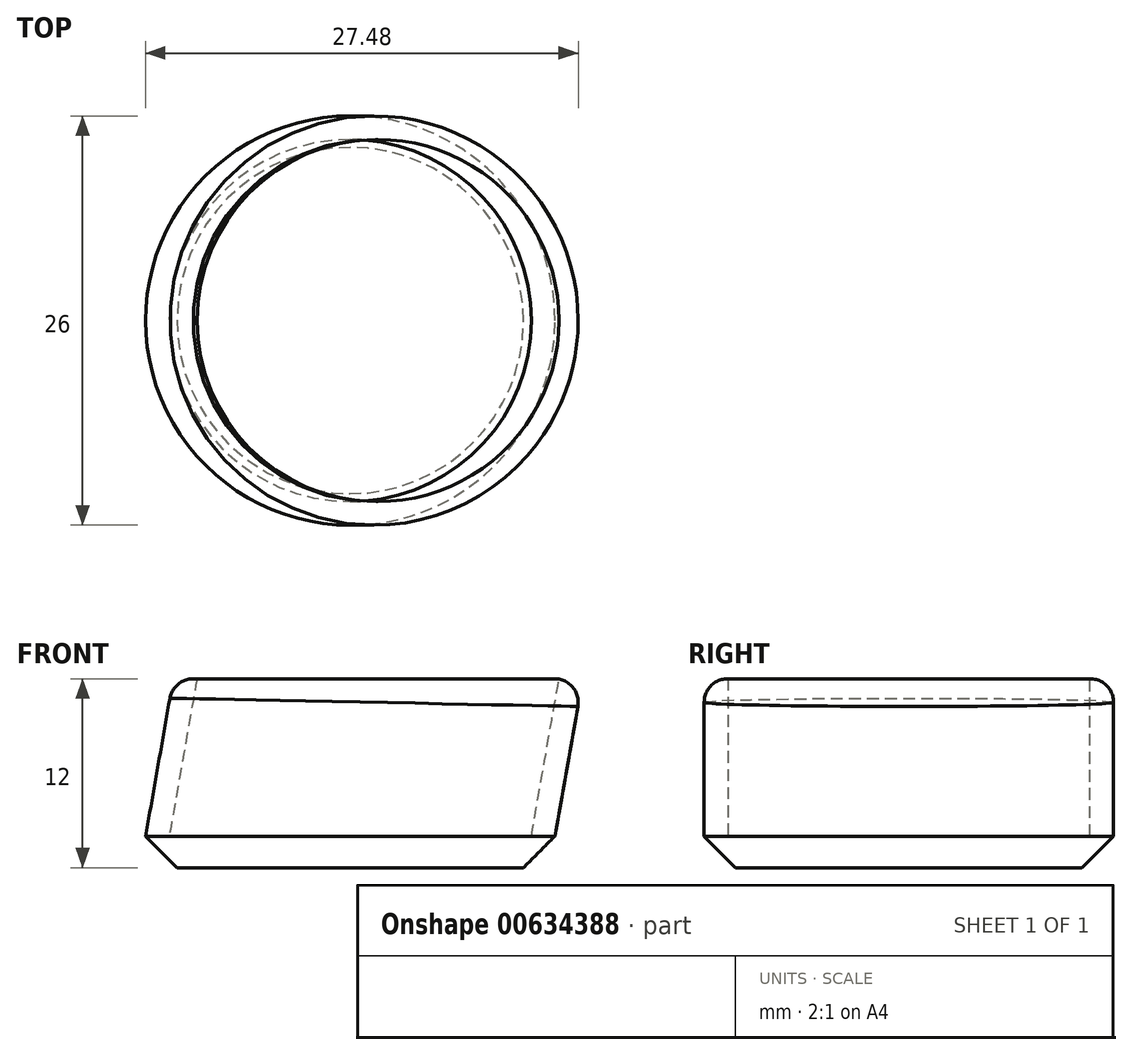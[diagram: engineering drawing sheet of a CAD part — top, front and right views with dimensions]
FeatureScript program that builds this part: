
annotation { "Feature Type Name" : "Feature", "Feature Type Description" : "" }
export const myFeature = defineFeature(function(context is Context, id is Id, definition is map)
    precondition{}
    {
        {
            var Q0;
            Q0=qCreatedBy(makeId("Front.planeOp"),FACE);
            var sketch = newSketch(context, id + "F0", { "sketchPlane" : qUnion([Q0])});
            skLineSegment(sketch, "E0", {"start": v(0, 0) * mm, "end": v(1.76, 10) * mm});
            skLineSegment(sketch, "E1", {"start": v(0, 0) * mm, "end": v(0, 10) * mm, "construction": true});
            skLineSegment(sketch, "E2", {"start": v(0, 10) * mm, "end": v(1.76, 10) * mm, "construction": true});
            skSolve(sketch);
        }
        {
            var Q0;
            Q0=qCreatedBy(makeId("Top.planeOp"),FACE);
            var sketch = newSketch(context, id + "F1", { "sketchPlane" : qUnion([Q0])});
            skCircle(sketch, "E3", {"center": v(0, 0) * mm, "radius": 13 * mm});
            skCircle(sketch, "E4", {"center": v(0, 0) * mm, "radius": 11.5 * mm});
            skSolve(sketch);
        }
        {
            var Q0;
            Q0=makeQuery(id+"F1.imprint","IMPRINT",FACE,{"disambiguationData":[TD([[makeQuery(id+"F1.imprint","IMPRINT",EDGE,{"derivedFrom":sQuery(id+"F1.wireOp",EDGE,"E3")}),1.0]])]});
            var Q1;
            Q1=sQuery(id+"F0.wireOp",EDGE,"E0");
            sweep(context, id + "F2", {"profiles" : qUnion([Q0]), "path" : qUnion([Q1])});
        }
        {
            var Q0;
            Q0=qCreatedBy(makeId("Top.planeOp"),FACE);
            var sketch = newSketch(context, id + "F3", { "sketchPlane" : qUnion([Q0])});
            skCircle(sketch, "E5.0", {"center": v(0, 0) * mm, "radius": 13 * mm});
            skSolve(sketch);
        }
        {
            var Q0;
            Q0=makeQuery(id+"F3.imprint","IMPRINT",FACE,{"disambiguationData":[TD([[makeQuery(id+"F3.imprint","IMPRINT",EDGE,{"derivedFrom":sQuery(id+"F3.wireOp",EDGE,"E5.0")}),1.0]])]});
            extrude(context, id + "F4", {"entities" : qUnion([Q0]), "operationType" : NewBodyOperationType.ADD, "oppositeDirection" : true, "depth" : 2 * mm, "offsetDistance" : 25 * mm});
        }
        {
            var Q0;
            Q0=makeQuery(id+"F2.opSweep","CAP_EDGE",EDGE,{"disambiguationData":[OSD([sQuery(id+"F0.wireOp",VERTEX,"E0.end"),sQuery(id+"F1.wireOp",EDGE,"E3")])],"isStart":false});
            fillet(context, id + "F5", {"entities" : qUnion([Q0]), "radius" : 1.5 * mm, "tangentPropagation" : true, "allowEdgeOverflow" : false});
        }
        {
            var Q0;
            Q0=makeQuery(id+"F4.opExtrude","CAP_EDGE",EDGE,{"disambiguationData":[OSD([sQuery(id+"F3.wireOp",EDGE,"E5.0")])],"isStart":false});
            chamfer(context, id + "F6", {"entities" : qUnion([Q0]), "width" : 2 * mm, "tangentPropagation" : true});
        }
    });
